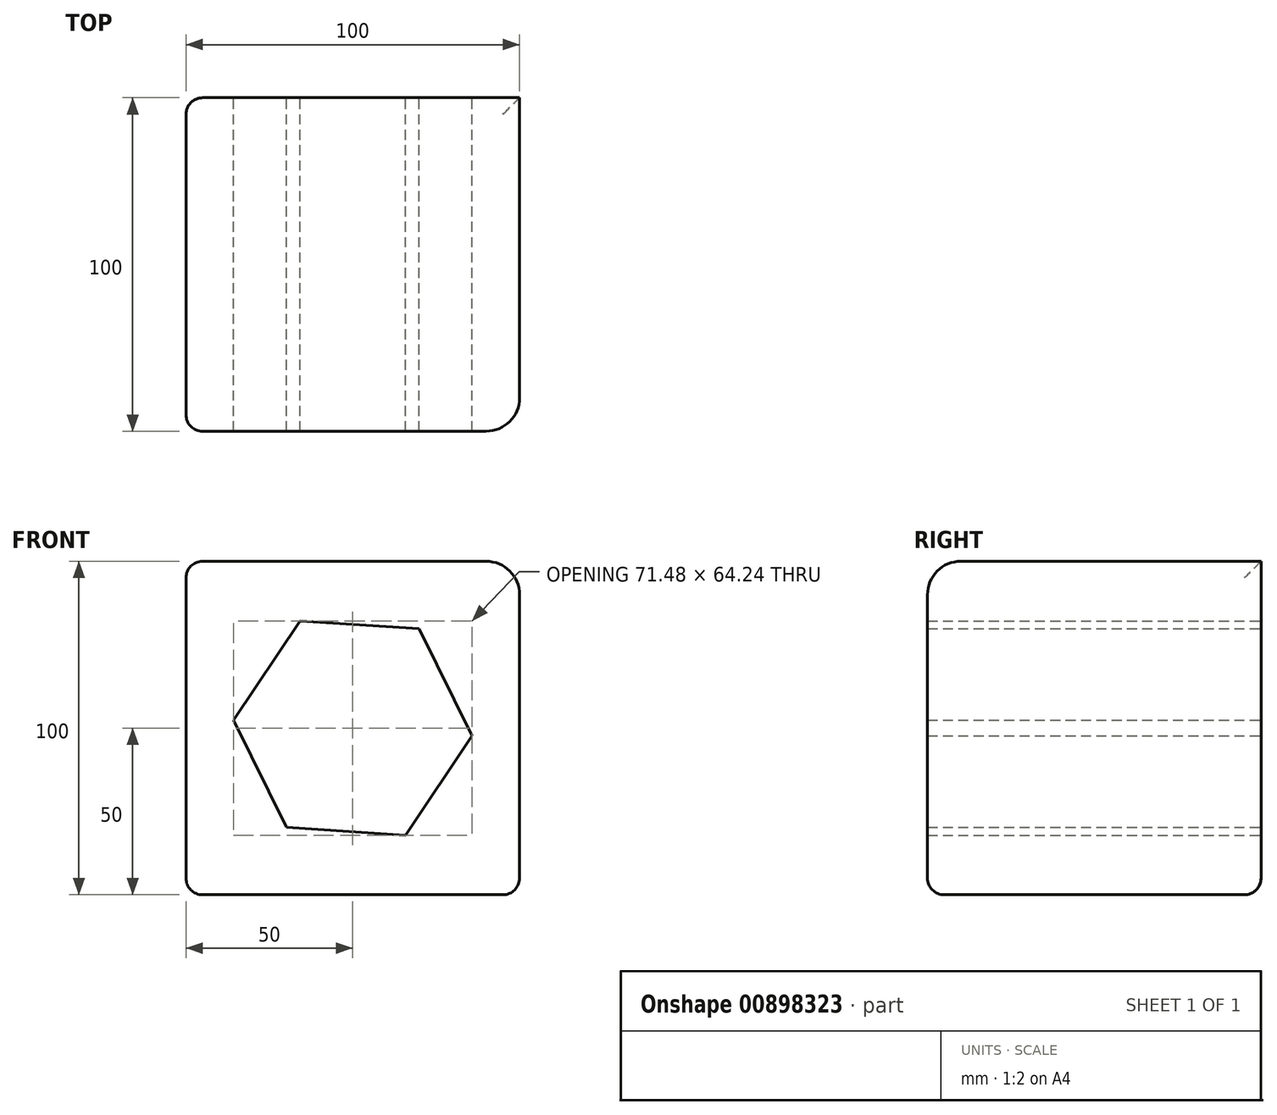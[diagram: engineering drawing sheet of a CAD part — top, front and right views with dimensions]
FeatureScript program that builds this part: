
annotation { "Feature Type Name" : "Feature", "Feature Type Description" : "" }
export const myFeature = defineFeature(function(context is Context, id is Id, definition is map)
    precondition{}
    {
        {
            var Q0;
            Q0=qCreatedBy(makeId("Front.planeOp"),FACE);
            var sketch = newSketch(context, id + "F0", { "sketchPlane" : qUnion([Q0])});
            skLineSegment(sketch, "E0.bottom", {"start": v(50, -50) * mm, "end": v(-50, -50) * mm});
            skLineSegment(sketch, "E0.top", {"start": v(50, 50) * mm, "end": v(-50, 50) * mm});
            skLineSegment(sketch, "E0.left", {"start": v(50, -50) * mm, "end": v(50, 50) * mm});
            skLineSegment(sketch, "E0.right", {"start": v(-50, -50) * mm, "end": v(-50, 50) * mm});
            skPoint(sketch, "E0.middle", {"position": v(0, 0) * mm});
            skSolve(sketch);
        }
        {
            var Q0;
            Q0=qCreatedBy(makeId("Front.planeOp"),FACE);
            var sketch = newSketch(context, id + "F1", { "sketchPlane" : qUnion([Q0])});
            skCircle(sketch, "E1.cCircle", {"center": v(0, 0) * mm, "radius": 35.81 * mm, "construction": true});
            skLineSegment(sketch, "E1.0", {"start": v(-15.84, 32.12) * mm, "end": v(19.9, 29.78) * mm});
            skLineSegment(sketch, "E1.1", {"start": v(19.9, 29.78) * mm, "end": v(35.74, -2.34) * mm});
            skLineSegment(sketch, "E1.2", {"start": v(35.74, -2.34) * mm, "end": v(15.84, -32.12) * mm});
            skLineSegment(sketch, "E1.3", {"start": v(15.84, -32.12) * mm, "end": v(-19.9, -29.78) * mm});
            skLineSegment(sketch, "E1.4", {"start": v(-19.9, -29.78) * mm, "end": v(-35.74, 2.34) * mm});
            skLineSegment(sketch, "E1.5", {"start": v(-35.74, 2.34) * mm, "end": v(-15.84, 32.12) * mm});
            skSolve(sketch);
        }
        {
            var Q0;
            Q0=makeQuery(id+"F0.imprint","IMPRINT",FACE,{"disambiguationData":[TD([[makeQuery(id+"F0.imprint","IMPRINT",EDGE,{"derivedFrom":sQuery(id+"F0.wireOp",EDGE,"E0.bottom")}),-1.0]])]});
            extrude(context, id + "F2", {"entities" : qUnion([Q0]), "depth" : 100 * mm, "offsetDistance" : 25 * mm});
        }
        {
            var Q0;
            Q0=makeQuery(id+"F1.imprint","IMPRINT",FACE,{"disambiguationData":[TD([[makeQuery(id+"F1.imprint","IMPRINT",EDGE,{"derivedFrom":sQuery(id+"F1.wireOp",EDGE,"E1.0")}),-1.0]])]});
            extrude(context, id + "F3", {"entities" : qUnion([Q0]), "operationType" : NewBodyOperationType.REMOVE, "depth" : 248 * mm, "offsetDistance" : 25 * mm});
        }
        {
            var Q0;
            Q0=makeQuery(id+"F2.opExtrude","SWEPT_EDGE",EDGE,{"disambiguationData":[OSD([sQuery(id+"F0.wireOp",EDGE,"E0.bottom"),sQuery(id+"F0.wireOp",EDGE,"E0.right")])]});
            var Q1;
            Q1=makeQuery(id+"F2.opExtrude","SWEPT_FACE",FACE,{"disambiguationData":[OSD([sQuery(id+"F0.wireOp",EDGE,"E0.bottom")])]});
            var Q2;
            Q2=makeQuery(id+"F2.opExtrude","SWEPT_FACE",FACE,{"disambiguationData":[OSD([sQuery(id+"F0.wireOp",EDGE,"E0.right")])]});
            var Q3;
            Q3=makeQuery(id+"F2.opExtrude","CAP_EDGE",EDGE,{"disambiguationData":[OSD([sQuery(id+"F0.wireOp",EDGE,"E0.right")])],"isStart":false});
            fillet(context, id + "F4", {"entities" : qUnion([Q0, Q1, Q2, Q3]), "radius" : 5 * mm, "tangentPropagation" : true, "allowEdgeOverflow" : false});
        }
        {
            var Q0;
            Q0=makeQuery(id+"F2.opExtrude","CAP_EDGE",EDGE,{"disambiguationData":[OSD([sQuery(id+"F0.wireOp",EDGE,"E0.top")])],"isStart":false});
            var Q1;
            Q1=makeQuery(id+"F2.opExtrude","CAP_EDGE",EDGE,{"disambiguationData":[OSD([sQuery(id+"F0.wireOp",EDGE,"E0.left")])],"isStart":false});
            var Q2;
            Q2=makeQuery(id+"F2.opExtrude","SWEPT_EDGE",EDGE,{"disambiguationData":[OSD([sQuery(id+"F0.wireOp",EDGE,"E0.top"),sQuery(id+"F0.wireOp",EDGE,"E0.left")])]});
            var Q3;
            {var subQ0=sQuery(id+"F0.wireOp",EDGE,"E0.top");Q3=makeQuery(id+"F4.opFillet","BLEND_EDGE",EDGE,{"blendedFrom":[makeQuery(id+"F2.opExtrude","SWEPT_EDGE",EDGE,{"disambiguationData":[OSD([subQ0,sQuery(id+"F0.wireOp",EDGE,"E0.right")])]}),makeQuery(id+"F2.opExtrude","SWEPT_FACE",FACE,{"disambiguationData":[OSD([subQ0])]})],"blendedInto":[makeQuery(id+"F2.opExtrude","SWEPT_FACE",FACE,{"disambiguationData":[OSD([subQ0])]})]});}
            fillet(context, id + "F5", {"entities" : qUnion([Q0, Q1, Q2, Q3]), "radius" : 10 * mm, "tangentPropagation" : true, "allowEdgeOverflow" : false});
        }
    });
